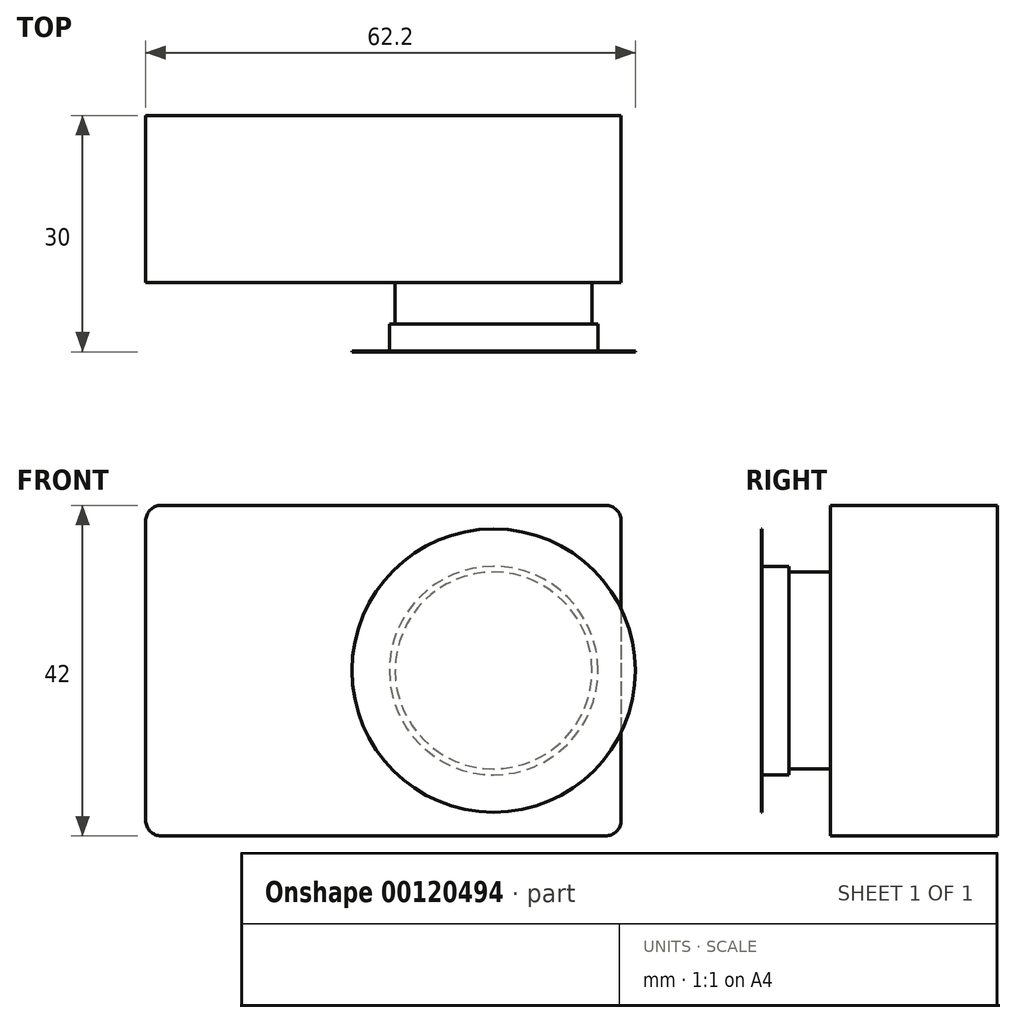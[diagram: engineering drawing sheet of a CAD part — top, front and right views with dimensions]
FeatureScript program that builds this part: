
annotation { "Feature Type Name" : "Feature", "Feature Type Description" : "" }
export const myFeature = defineFeature(function(context is Context, id is Id, definition is map)
    precondition{}
    {
        {
            var Q0;
            Q0=qCreatedBy(makeId("Front.planeOp"),FACE);
            var sketch = newSketch(context, id + "F0", { "sketchPlane" : qUnion([Q0])});
            skLineSegment(sketch, "E0", {"start": v(30.2, 0) * mm, "end": v(30.2, 21) * mm});
            skLineSegment(sketch, "E1", {"start": v(30.2, 21) * mm, "end": v(-30.2, 21) * mm});
            skLineSegment(sketch, "E2", {"start": v(-30.2, 21) * mm, "end": v(-30.2, -21) * mm});
            skLineSegment(sketch, "E3", {"start": v(-30.2, -21) * mm, "end": v(30.2, -21) * mm});
            skLineSegment(sketch, "E4", {"start": v(30.2, 0) * mm, "end": v(30.2, -21) * mm});
            skLineSegment(sketch, "E5", {"start": v(0, 0) * mm, "end": v(14, 0) * mm, "construction": true});
            skCircle(sketch, "E6", {"center": v(14, 0) * mm, "radius": 12.5 * mm});
            skSolve(sketch);
        }
        {
            var Q0;
            Q0=makeQuery(id+"F0.imprint","IMPRINT",FACE,{"disambiguationData":[TD([[makeQuery(id+"F0.imprint","IMPRINT",EDGE,{"derivedFrom":sQuery(id+"F0.wireOp",EDGE,"E6")}),1.0]])]});
            extrude(context, id + "F1", {"entities" : qUnion([Q0]), "depth" : 30 * mm});
        }
        {
            var Q0;
            Q0 = qSketchRegion(id + "F0", true);
            extrude(context, id + "F2", {"entities" : qUnion([Q0]), "operationType" : NewBodyOperationType.ADD, "depth" : 21.2 * mm});
        }
        {
            var Q0;
            Q0=makeQuery(id+"F2.opExtrude","SWEPT_EDGE",EDGE,{"disambiguationData":[OSD([sQuery(id+"F0.wireOp",EDGE,"E1"),sQuery(id+"F0.wireOp",EDGE,"E2")])]});
            fillet(context, id + "F3", {"entities" : qUnion([Q0]), "radius" : 2 * mm, "tangentPropagation" : true, "allowEdgeOverflow" : false});
        }
        {
            var Q0;
            Q0=makeQuery(id+"F2.opExtrude","SWEPT_EDGE",EDGE,{"disambiguationData":[OSD([sQuery(id+"F0.wireOp",EDGE,"E0"),sQuery(id+"F0.wireOp",EDGE,"E1")])]});
            fillet(context, id + "F4", {"entities" : qUnion([Q0]), "radius" : 2 * mm, "tangentPropagation" : true, "allowEdgeOverflow" : false});
        }
        {
            var Q0;
            Q0=makeQuery(id+"F2.opExtrude","SWEPT_EDGE",EDGE,{"disambiguationData":[OSD([sQuery(id+"F0.wireOp",EDGE,"E2"),sQuery(id+"F0.wireOp",EDGE,"E3")])]});
            fillet(context, id + "F5", {"entities" : qUnion([Q0]), "radius" : 2 * mm, "tangentPropagation" : true, "allowEdgeOverflow" : false});
        }
        {
            var Q0;
            Q0=makeQuery(id+"F2.opExtrude","SWEPT_EDGE",EDGE,{"disambiguationData":[OSD([sQuery(id+"F0.wireOp",EDGE,"E3"),sQuery(id+"F0.wireOp",EDGE,"E4")])]});
            fillet(context, id + "F6", {"entities" : qUnion([Q0]), "radius" : 2 * mm, "tangentPropagation" : true, "allowEdgeOverflow" : false});
        }
        {
            var Q0;
            Q0=makeQuery(id+"F1.opExtrude","CAP_FACE",FACE,{"disambiguationData":[OSD([sQuery(id+"F0.wireOp",EDGE,"E6")])],"isStart":false});
            var sketch = newSketch(context, id + "F7", { "sketchPlane" : qUnion([Q0])});
            skCircle(sketch, "E7", {"center": v(14, 0) * mm, "radius": 18 * mm});
            skCircle(sketch, "E8", {"center": v(14, 0) * mm, "radius": 13.25 * mm});
            skCircle(sketch, "E9", {"center": v(14, 0) * mm, "radius": 17.5 * mm});
            skSolve(sketch);
        }
        {
            var Q0;
            Q0=makeQuery(id+"F7.imprint","IMPRINT",FACE,{"disambiguationData":[TD([[makeQuery(id+"F7.imprint","IMPRINT",EDGE,{"derivedFrom":sQuery(id+"F7.wireOp",EDGE,"E8")}),1.0]])]});
            extrude(context, id + "F8", {"entities" : qUnion([Q0]), "operationType" : NewBodyOperationType.ADD, "oppositeDirection" : true, "depth" : 3.5 * mm});
        }
        {
            var Q0;
            Q0=sQuery(id+"F7.wireOp",EDGE,"E7");
            var Q1;
            Q1=sQuery(id+"F7.wireOp",EDGE,"E9");
            extrude(context, id + "F9", {"bodyType" : ToolBodyType.SURFACE, "surfaceEntities" : qUnion([Q0, Q1]), "depth" : 3 * mm});
        }
        {
            var Q0;
            Q0=makeQuery(id+"F7.imprint","IMPRINT",FACE,{"disambiguationData":[TD([[makeQuery(id+"F7.imprint","IMPRINT",EDGE,{"derivedFrom":sQuery(id+"F7.wireOp",EDGE,"E8")}),-1.0]])]});
            var Q1;
            Q1=makeQuery(id+"F7.imprint","IMPRINT",FACE,{"disambiguationData":[TD([[makeQuery(id+"F7.imprint","IMPRINT",EDGE,{"derivedFrom":sQuery(id+"F7.wireOp",EDGE,"E7")}),1.0]])]});
            extrude(context, id + "F10", {"entities" : qUnion([Q0, Q1]), "operationType" : NewBodyOperationType.ADD, "oppositeDirection" : true, "depth" : 0.1 * mm});
        }
    });
